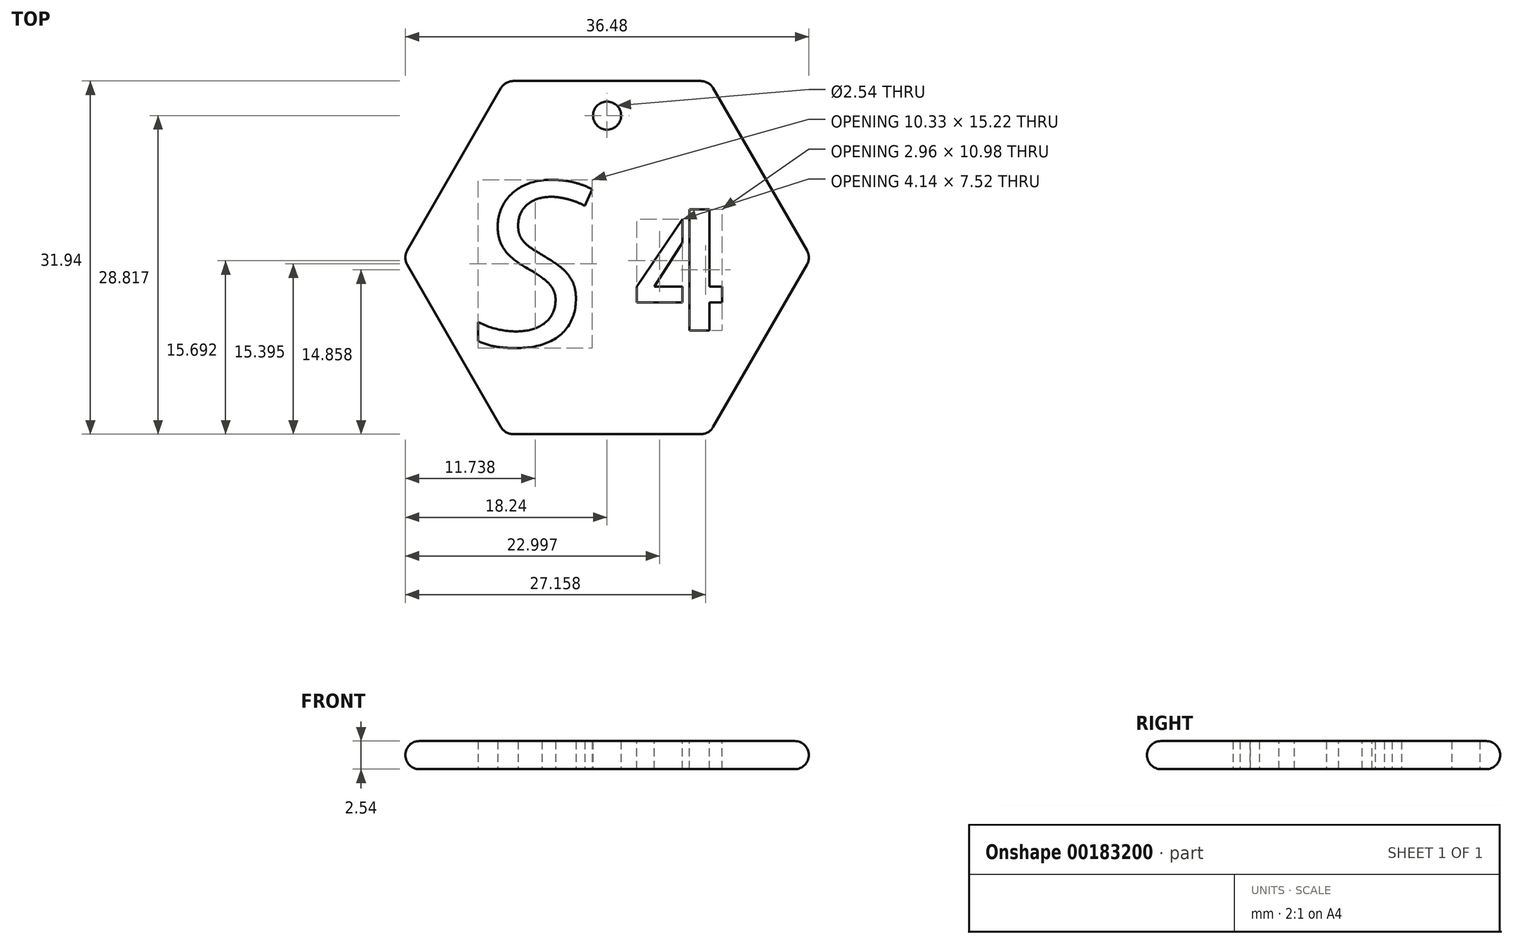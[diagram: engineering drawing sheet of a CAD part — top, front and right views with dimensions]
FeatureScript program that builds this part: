
annotation { "Feature Type Name" : "Feature", "Feature Type Description" : "" }
export const myFeature = defineFeature(function(context is Context, id is Id, definition is map)
    precondition{}
    {
        {
            var Q0;
            Q0=qCreatedBy(makeId("Top.planeOp"),FACE);
            var sketch = newSketch(context, id + "F0", { "sketchPlane" : qUnion([Q0])});
            skCircle(sketch, "E0.cCircle", {"center": v(0, 0) * mm, "radius": 15.97 * mm, "construction": true});
            skLineSegment(sketch, "E0.0", {"start": v(9.22, -15.97) * mm, "end": v(-9.22, -15.97) * mm});
            skLineSegment(sketch, "E0.1", {"start": v(-9.22, -15.97) * mm, "end": v(-18.44, 0) * mm});
            skLineSegment(sketch, "E0.2", {"start": v(-18.44, 0) * mm, "end": v(-9.22, 15.97) * mm});
            skLineSegment(sketch, "E0.3", {"start": v(-9.22, 15.97) * mm, "end": v(9.22, 15.97) * mm});
            skLineSegment(sketch, "E0.4", {"start": v(9.22, 15.97) * mm, "end": v(18.44, 0) * mm});
            skLineSegment(sketch, "E0.5", {"start": v(18.44, 0) * mm, "end": v(9.22, -15.97) * mm});
            skPoint(sketch, "E0.0.midPoint", {"position": v(0, -15.97) * mm});
            skSolve(sketch);
        }
        {
            var Q0;
            Q0=qCreatedBy(makeId("Top.planeOp"),FACE);
            var sketch = newSketch(context, id + "F1", { "sketchPlane" : qUnion([Q0])});
            skText(sketch, "E1", { "text": "S", "fontName": "OpenSans-Italic.ttf"});
            const initialGuessF1  = {"E1": [-0.01206, -0.00798, 1, 0, 0.01493]};
            skSetInitialGuess(sketch, initialGuessF1);
            skSolve(sketch);
        }
        {
            var Q0;
            Q0=makeQuery(id+"F0.imprint","IMPRINT",FACE,{"disambiguationData":[TD([[makeQuery(id+"F0.imprint","IMPRINT",EDGE,{"derivedFrom":sQuery(id+"F0.wireOp",EDGE,"E0.0")}),-1.0]])]});
            extrude(context, id + "F2", {"entities" : qUnion([Q0]), "depth" : 2.54 * mm});
        }
        {
            var Q0;
            Q0 = qSketchRegion(id + "F1", true);
            extrude(context, id + "F3", {"entities" : qUnion([Q0]), "operationType" : NewBodyOperationType.REMOVE, "depth" : 5.08 * mm});
        }
        {
            var Q0;
            Q0=qCreatedBy(makeId("Top.planeOp"),FACE);
            var sketch = newSketch(context, id + "F4", { "sketchPlane" : qUnion([Q0])});
            skPoint(sketch, "E2", {"position": v(0, 12.85) * mm});
            skSolve(sketch);
        }
        {
            var Q0;
            Q0=sQuery(id+"F4.wireOp",VERTEX,"E2");
            var Q1;
            Q1=makeQuery(id+"FmSMFXF0oAyxUw3_1.boolean.opBoolean","SPLIT",BODY,{"disambiguationData":[OD(0.0)],"derivedFrom":makeQuery(id+"F2.opExtrude","SWEPT_BODY",BODY,{"disambiguationData":[OSD([sQuery(id+"F0.wireOp",EDGE,"E0.0"),sQuery(id+"F0.wireOp",EDGE,"E0.1"),sQuery(id+"F0.wireOp",EDGE,"E0.2"),sQuery(id+"F0.wireOp",EDGE,"E0.3"),sQuery(id+"F0.wireOp",EDGE,"E0.4"),sQuery(id+"F0.wireOp",EDGE,"E0.5")])]})});
            hole(context, id + "F5", {"style" : HoleStyle.SIMPLE, "endStyle" : HoleEndStyle.THROUGH, "oppositeDirection" : true, "holeDiameter" : 2.54 * mm, "locations" : qUnion([Q0]), "scope" : qUnion([Q1]), "isTappedThrough" : true});
        }
        {
            var Q0;
            Q0=makeQuery(id+"F2.opExtrude","CAP_EDGE",EDGE,{"disambiguationData":[OSD([sQuery(id+"F0.wireOp",EDGE,"E0.4")])],"isStart":true});
            var Q1;
            Q1=makeQuery(id+"F2.opExtrude","CAP_EDGE",EDGE,{"disambiguationData":[OSD([sQuery(id+"F0.wireOp",EDGE,"E0.5")])],"isStart":false});
            var Q2;
            Q2=makeQuery(id+"F2.opExtrude","CAP_EDGE",EDGE,{"disambiguationData":[OSD([sQuery(id+"F0.wireOp",EDGE,"E0.3")])],"isStart":false});
            var Q3;
            Q3=makeQuery(id+"F2.opExtrude","CAP_EDGE",EDGE,{"disambiguationData":[OSD([sQuery(id+"F0.wireOp",EDGE,"E0.0")])],"isStart":true});
            var Q4;
            Q4=makeQuery(id+"F2.opExtrude","CAP_EDGE",EDGE,{"disambiguationData":[OSD([sQuery(id+"F0.wireOp",EDGE,"E0.0")])],"isStart":false});
            var Q5;
            Q5=makeQuery(id+"F2.opExtrude","SWEPT_FACE",FACE,{"disambiguationData":[OSD([sQuery(id+"F0.wireOp",EDGE,"E0.1")])]});
            var Q6;
            Q6=makeQuery(id+"F2.opExtrude","SWEPT_FACE",FACE,{"disambiguationData":[OSD([sQuery(id+"F0.wireOp",EDGE,"E0.0")])]});
            var Q7;
            Q7=makeQuery(id+"F2.opExtrude","SWEPT_FACE",FACE,{"disambiguationData":[OSD([sQuery(id+"F0.wireOp",EDGE,"E0.3")])]});
            var Q8;
            Q8=makeQuery(id+"F2.opExtrude","CAP_EDGE",EDGE,{"disambiguationData":[OSD([sQuery(id+"F0.wireOp",EDGE,"E0.4")])],"isStart":false});
            var Q9;
            Q9=makeQuery(id+"F2.opExtrude","CAP_EDGE",EDGE,{"disambiguationData":[OSD([sQuery(id+"F0.wireOp",EDGE,"E0.2")])],"isStart":true});
            var Q10;
            Q10=makeQuery(id+"F2.opExtrude","CAP_EDGE",EDGE,{"disambiguationData":[OSD([sQuery(id+"F0.wireOp",EDGE,"E0.2")])],"isStart":false});
            var Q11;
            Q11=makeQuery(id+"F2.opExtrude","SWEPT_FACE",FACE,{"disambiguationData":[OSD([sQuery(id+"F0.wireOp",EDGE,"E0.5")])]});
            fillet(context, id + "F6", {"entities" : qUnion([Q0, Q1, Q2, Q3, Q4, Q5, Q6, Q7, Q8, Q9, Q10, Q11]), "radius" : 1.27 * mm, "tangentPropagation" : true, "allowEdgeOverflow" : false});
        }
        {
            var Q0;
            Q0=makeQuery(id+"F2.opExtrude","CAP_FACE",FACE,{"disambiguationData":[OSD([sQuery(id+"F0.wireOp",EDGE,"E0.0"),sQuery(id+"F0.wireOp",EDGE,"E0.1"),sQuery(id+"F0.wireOp",EDGE,"E0.2"),sQuery(id+"F0.wireOp",EDGE,"E0.3"),sQuery(id+"F0.wireOp",EDGE,"E0.4"),sQuery(id+"F0.wireOp",EDGE,"E0.5")])],"isStart":false});
            var sketch = newSketch(context, id + "F7", { "sketchPlane" : qUnion([Q0])});
            skText(sketch, "E3", { "text": "4", "fontName": "AllertaStencil-Regular.ttf"});
            const initialGuessF7  = {"E3": [0.00212, -0.0066, 1, 0, 0.01098]};
            skSetInitialGuess(sketch, initialGuessF7);
            skSolve(sketch);
        }
        {
            var Q0;
            Q0=makeQuery(id+"F7.imprint","IMPRINT",FACE,{"disambiguationData":[TD([[makeQuery(id+"F7.imprint","IMPRINT",EDGE,{"derivedFrom":sQuery(id+"F7.wireOp",EDGE,"E3.sketch_text.stroke-8")}),-1.0]])]});
            var Q1;
            Q1=makeQuery(id+"F7.imprint","IMPRINT",FACE,{"disambiguationData":[TD([[makeQuery(id+"F7.imprint","IMPRINT",EDGE,{"derivedFrom":sQuery(id+"F7.wireOp",EDGE,"E3.sketch_text.stroke-0")}),-1.0]])]});
            extrude(context, id + "F8", {"entities" : qUnion([Q0, Q1]), "operationType" : NewBodyOperationType.REMOVE, "oppositeDirection" : true, "depth" : 2.54 * mm});
        }
    });
